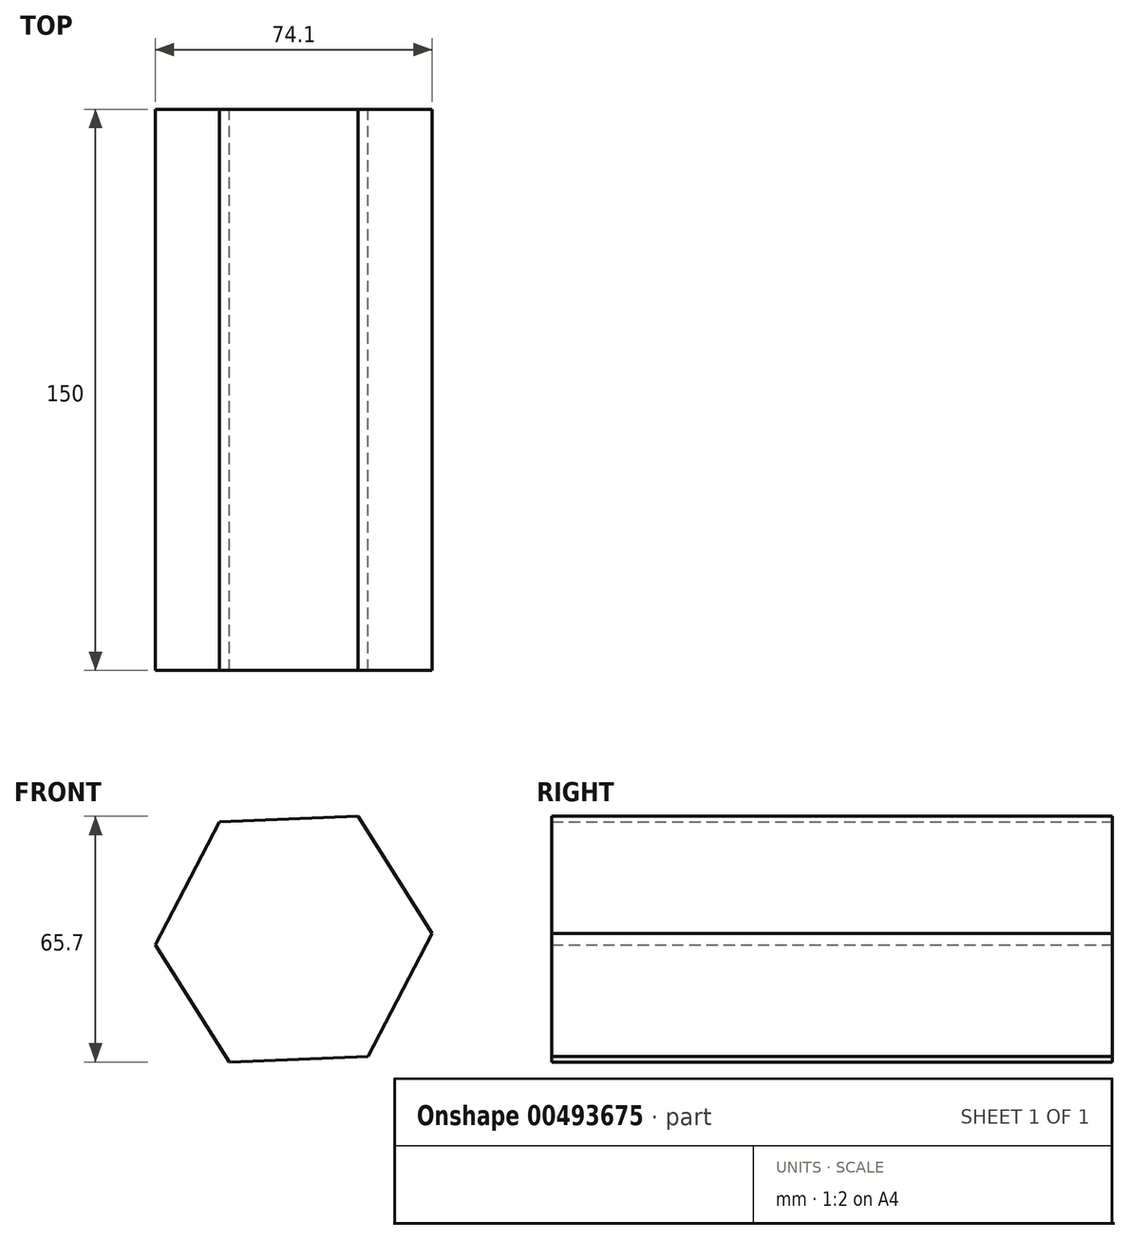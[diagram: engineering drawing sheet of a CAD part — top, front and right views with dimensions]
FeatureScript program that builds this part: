
annotation { "Feature Type Name" : "Feature", "Feature Type Description" : "" }
export const myFeature = defineFeature(function(context is Context, id is Id, definition is map)
    precondition{}
    {
        {
            var Q0;
            Q0=qCreatedBy(makeId("Front.planeOp"),FACE);
            var sketch = newSketch(context, id + "F0", { "sketchPlane" : qUnion([Q0])});
            skCircle(sketch, "E0.cCircle", {"center": v(0, 0) * mm, "radius": 37.09 * mm, "construction": true});
            skLineSegment(sketch, "E0.0", {"start": v(17.21, 32.85) * mm, "end": v(37.05, 1.52) * mm});
            skLineSegment(sketch, "E0.1", {"start": v(37.05, 1.52) * mm, "end": v(19.84, -31.33) * mm});
            skLineSegment(sketch, "E0.2", {"start": v(19.84, -31.33) * mm, "end": v(-17.21, -32.85) * mm});
            skLineSegment(sketch, "E0.3", {"start": v(-17.21, -32.85) * mm, "end": v(-37.05, -1.52) * mm});
            skLineSegment(sketch, "E0.4", {"start": v(-37.05, -1.52) * mm, "end": v(-19.84, 31.33) * mm});
            skLineSegment(sketch, "E0.5", {"start": v(-19.84, 31.33) * mm, "end": v(17.21, 32.85) * mm});
            skSolve(sketch);
        }
        {
            var Q0;
            Q0=makeQuery(id+"F0.imprint","IMPRINT",FACE,{"disambiguationData":[TD([[makeQuery(id+"F0.imprint","IMPRINT",EDGE,{"derivedFrom":sQuery(id+"F0.wireOp",EDGE,"E0.0")}),-1.0]])]});
            extrude(context, id + "F1", {"entities" : qUnion([Q0]), "depth" : 150 * mm});
        }
    });
